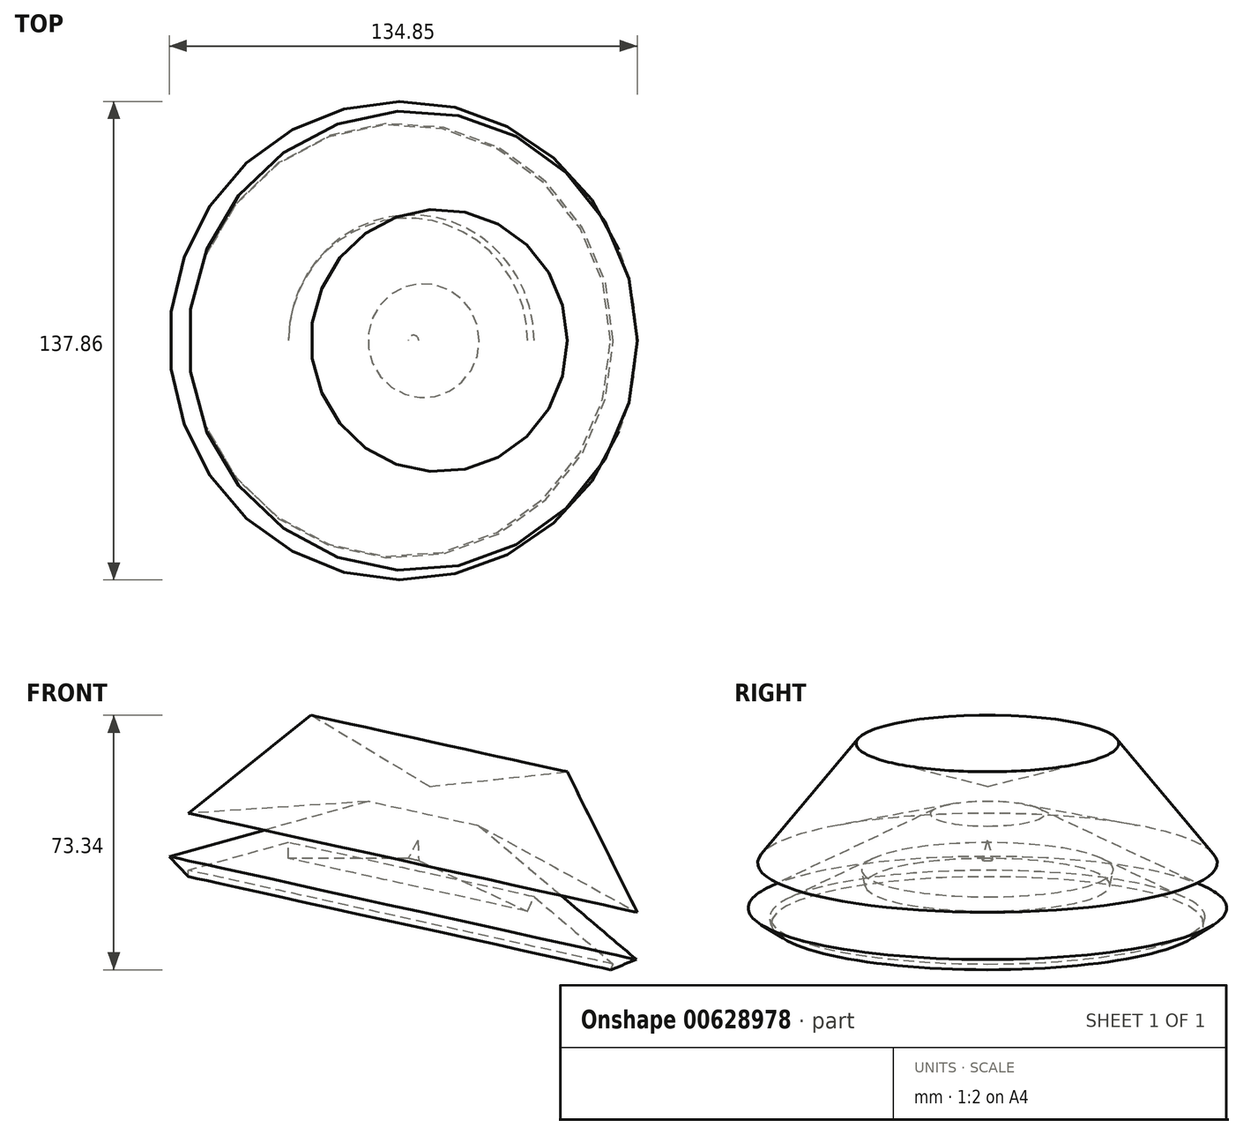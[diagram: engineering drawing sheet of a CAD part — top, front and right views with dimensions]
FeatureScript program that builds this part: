
annotation { "Feature Type Name" : "Feature", "Feature Type Description" : "" }
export const myFeature = defineFeature(function(context is Context, id is Id, definition is map)
    precondition{}
    {
        {
            var Q0;
            Q0=qCreatedBy(makeId("Front.planeOp"),FACE);
            var sketch = newSketch(context, id + "F0", { "sketchPlane" : qUnion([Q0])});
            skLineSegment(sketch, "E0", {"start": v(0, -24.73) * mm, "end": v(0, -29.3) * mm});
            skLineSegment(sketch, "E1", {"start": v(0, -29.3) * mm, "end": v(34.53, -29.3) * mm});
            skLineSegment(sketch, "E2", {"start": v(34.53, -29.3) * mm, "end": v(37.27, -24.05) * mm});
            skLineSegment(sketch, "E3", {"start": v(0, -24.73) * mm, "end": v(-28.84, -32.71) * mm});
            skLineSegment(sketch, "E4", {"start": v(-28.84, -16.3) * mm, "end": v(22.9, -12.88) * mm});
            skLineSegment(sketch, "E5", {"start": v(22.9, -12.88) * mm, "end": v(-34.35, -28.72) * mm});
            skPoint(sketch, "E5.endSnap0", {"position": v(-14.42, -28.72) * mm});
            skLineSegment(sketch, "E6", {"start": v(-34.35, -28.72) * mm, "end": v(-28.84, -34.53) * mm});
            skLineSegment(sketch, "E7", {"start": v(-28.84, -34.53) * mm, "end": v(-28.84, -32.71) * mm});
            skLineSegment(sketch, "E8", {"start": v(-28.84, -16.3) * mm, "end": v(6.5, 11.97) * mm});
            skLineSegment(sketch, "E9", {"start": v(6.5, 11.97) * mm, "end": v(40.69, -8.55) * mm});
            skLineSegment(sketch, "E10", {"start": v(40.69, -8.55) * mm, "end": v(37.27, -24.05) * mm});
            skSolve(sketch);
        }
        {
            var Q0;
            Q0=makeQuery(id+"F0.imprint","IMPRINT",FACE,{"disambiguationData":[TD([[makeQuery(id+"F0.imprint","IMPRINT",EDGE,{"derivedFrom":sQuery(id+"F0.wireOp",EDGE,"E0")}),1.0]])]});
            var Q1;
            Q1=sQuery(id+"F0.wireOp",EDGE,"E10");
            revolve(context, id + "F1", {"entities" : qUnion([Q0]), "axis" : qUnion([Q1]), "revolveType" : RevolveType.FULL});
        }
    });
